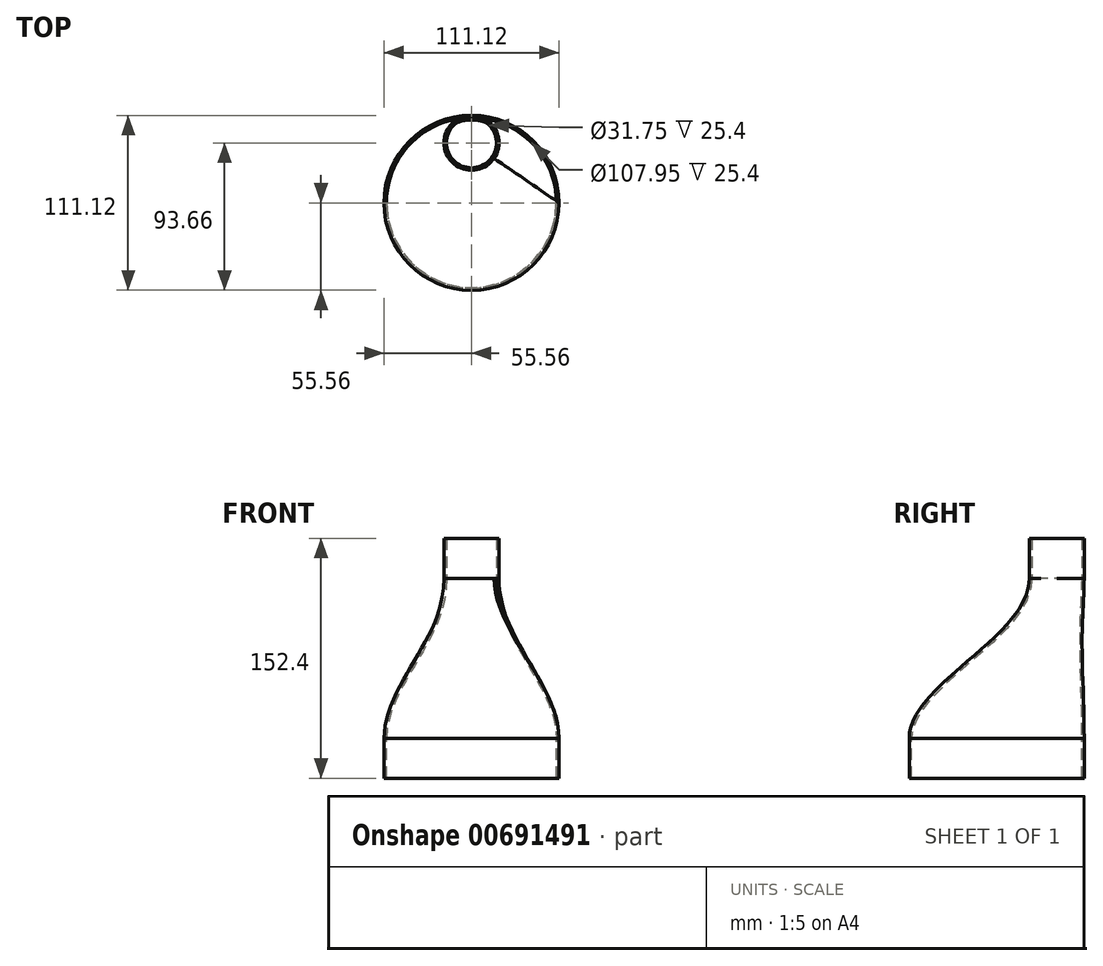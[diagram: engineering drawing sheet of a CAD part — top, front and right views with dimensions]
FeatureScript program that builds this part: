
annotation { "Feature Type Name" : "Feature", "Feature Type Description" : "" }
export const myFeature = defineFeature(function(context is Context, id is Id, definition is map)
    precondition{}
    {
        {
            var Q0;
            Q0=qCreatedBy(makeId("Top.planeOp"),FACE);
            var sketch = newSketch(context, id + "F0", { "sketchPlane" : qUnion([Q0])});
            skCircle(sketch, "E0", {"center": v(0, 0) * mm, "radius": 55.56 * mm});
            skSolve(sketch);
        }
        {
            var Q0;
            Q0=qCreatedBy(makeId("Top.planeOp"),FACE);
            cPlane(context, id + "F1", {"entities" : qUnion([Q0]), "cplaneType" : CPlaneType.OFFSET, "offset" : 101.6 * mm, "width" : 152.4 * mm, "height" : 152.4 * mm});
        }
        {
            var Q0;
            Q0=qCreatedBy(id+"F1.planeOp",FACE);
            var sketch = newSketch(context, id + "F2", { "sketchPlane" : qUnion([Q0])});
            skCircle(sketch, "E1", {"center": v(0, 38.1) * mm, "radius": 17.46 * mm});
            skSolve(sketch);
        }
        {
            var Q0;
            Q0=makeQuery(id+"F0.imprint","IMPRINT",FACE,{"disambiguationData":[TD([[makeQuery(id+"F0.imprint","IMPRINT",EDGE,{"derivedFrom":sQuery(id+"F0.wireOp",EDGE,"E0")}),1.0]])]});
            var Q1;
            Q1=makeQuery(id+"F2.imprint","IMPRINT",FACE,{"disambiguationData":[TD([[makeQuery(id+"F2.imprint","IMPRINT",EDGE,{"derivedFrom":sQuery(id+"F2.wireOp",EDGE,"E1")}),1.0]])]});
            var Q2;
            Q2=sQuery(id+"F0.wireOp",EDGE,"E0");
            var Q3;
            Q3=sQuery(id+"F2.wireOp",EDGE,"E1");
            loft(context, id + "F3", {"startCondition" : LoftEndDerivativeType.NORMAL_TO_PROFILE, "startMagnitude" : 1, "endCondition" : LoftEndDerivativeType.NORMAL_TO_PROFILE, "endMagnitude" : 1, "sheetProfilesArray" : [{ "sheetProfileEntities" : qUnion([Q0]) }, { "sheetProfileEntities" : qUnion([Q1]) }], "wireProfilesArray" : [{ "wireProfileEntities" : qUnion([Q2]) }, { "wireProfileEntities" : qUnion([Q3]) }]});
        }
        {
            var Q0;
            Q0=makeQuery(id+"F3.opLoft","CAP_FACE",FACE,{"disambiguationData":[OSD([makeQuery(id+"F0.imprint","IMPRINT",FACE,{"disambiguationData":[TD([[makeQuery(id+"F0.imprint","IMPRINT",EDGE,{"derivedFrom":sQuery(id+"F0.wireOp",EDGE,"E0")}),1.0]])]})])],"isStart":true});
            var Q1;
            Q1=makeQuery(id+"F3.opLoft","CAP_FACE",FACE,{"disambiguationData":[OSD([makeQuery(id+"F2.imprint","IMPRINT",FACE,{"disambiguationData":[TD([[makeQuery(id+"F2.imprint","IMPRINT",EDGE,{"derivedFrom":sQuery(id+"F2.wireOp",EDGE,"E1")}),1.0]])]})])],"isStart":true});
            shell(context, id + "F4", {"entities" : qUnion([Q0, Q1]), "thickness" : 1.59 * mm});
        }
        {
            var Q0;
            Q0=makeQuery(id+"F3.opLoft","CAP_FACE",FACE,{"disambiguationData":[OSD([makeQuery(id+"F2.imprint","IMPRINT",FACE,{"disambiguationData":[TD([[makeQuery(id+"F2.imprint","IMPRINT",EDGE,{"derivedFrom":sQuery(id+"F2.wireOp",EDGE,"E1")}),1.0]])]})])],"isStart":true});
            extrude(context, id + "F5", {"entities" : qUnion([Q0]), "operationType" : NewBodyOperationType.ADD, "depth" : 25.4 * mm, "offsetDistance" : 25.4 * mm});
        }
        {
            var Q0;
            Q0=makeQuery(id+"F3.opLoft","CAP_FACE",FACE,{"disambiguationData":[OSD([makeQuery(id+"F0.imprint","IMPRINT",FACE,{"disambiguationData":[TD([[makeQuery(id+"F0.imprint","IMPRINT",EDGE,{"derivedFrom":sQuery(id+"F0.wireOp",EDGE,"E0")}),1.0]])]})])],"isStart":true});
            extrude(context, id + "F6", {"entities" : qUnion([Q0]), "operationType" : NewBodyOperationType.ADD, "depth" : 25.4 * mm, "offsetDistance" : 25.4 * mm});
        }
    });
